# Revit family: IS_Tempo_T6973_BIM_GB
name_source: partatom
category: Plumbing Fixtures
revit_build: Autodesk Revit MEP 2012 (Build: 20110309_2315(x64)
units: mm (PartAtom-declared; Revit-internal decimal feet)

## types (1)
- T679301 - Tempo Seat & Cover, Slow Close
    Accessories = www.idealspec.co.uk
    AreaUnits = millimeters
    Assembly Code = C1030200
    AssetType = Fixed
    BIMObjectName = ISI_IdealStandard_WCSeat_Tempo_T6793
    Brand = Ideal Standard
    CWFU = 0
    Color = White
    ConnectionType = Plumbing
    Cost = 0 $
    Default Elevation = 1219 mm
    Description = Tempo seat & cover,  slow close
    DurationUnit = year
    ECA = No
    ExpectedLife = 15
    Features = Slow close
    Finish = White
    HWFU = 0
    Help = www.idealspec.co.uk/contact-us.html
    IfcExportAs = IfcSanitaryTerminalType
    IfcExportType = WCSEAT
    InstallationInstructions = www.idealspec.co.uk/resources.html
    LinearUnits = millimeters
    ManufacturerURL = www.idealspec.co.uk
    Material = Plastic
    Model = T679301
    ModelNumber = T679301
    ModelReference = Tempo seat & cover,  slow close
    NBSDescription = WC seats and covers
    NBSReference = 45-35-70/391
    Name = WCSeats_Tempo-AllVariants_IdealStandard
    NettWeight = 2.3 Kg
    NominalDepth = 425 mm
    NominalHeight = 40 mm  [stored 0.131234 ft]
    NominalLength = 425 mm
    NominalWidth = 358 mm
    ProductInformation = www.idealspec.co.uk/assets/datasheet/T679301
    SeatColor = White
    SeatHasCover = Yes
    SeatMaterial = Plastic
    SeatSKU = ISI_IdealStandard_WCSeat_SeatMaterial_Render
    SeatType = RingSeat
    Shape = Soft Square
    Size = 425 x 358 x 40 mm
    Space = Internal
    SpareParts = www.fastpart-spares.co.uk
    URL = www.idealspec.co.uk
    Uniclass2 = Pr_40_20_93_95
    Version = 2
    VolumeUnits = Litres
    WFU = 0
    WRAS = No
    WarrantyDescription = Manufacturers Warranty
    WarrantyDurationParts = 5
    WarrantyDurationUnit = year
    WaterEfficientProduct = No

note: [stored X ft] marks values corroborated as IEEE doubles in the binary element streams (Revit-internal decimal feet)

## geometry (parser evidence)
native form markers: Blend x3, Sweep x5
no freeform markers — native parametric forms only
